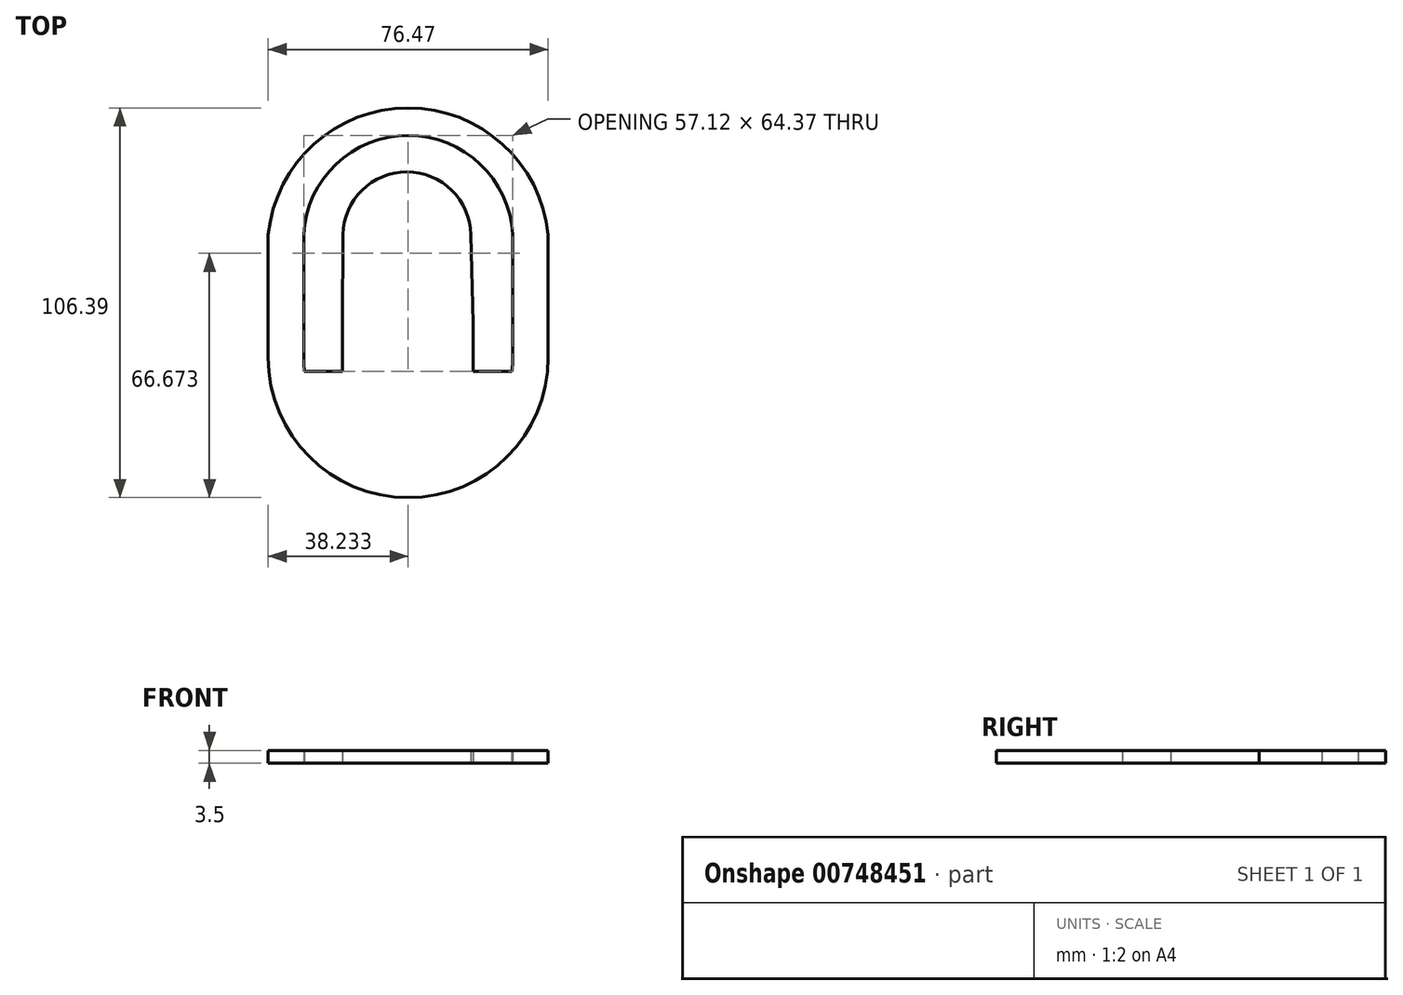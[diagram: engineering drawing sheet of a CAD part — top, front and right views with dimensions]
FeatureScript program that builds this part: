
annotation { "Feature Type Name" : "Feature", "Feature Type Description" : "" }
export const myFeature = defineFeature(function(context is Context, id is Id, definition is map)
    precondition{}
    {
        {
            var Q0;
            Q0=qCreatedBy(makeId("Top.planeOp"),FACE);
            var sketch = newSketch(context, id + "F0", { "sketchPlane" : qUnion([Q0])});
            skArc(sketch, "E0", {"start": v(10.8, 41.88) * mm, "mid": v(-1.53, 54.45) * mm, "end": v(-13.07, 41.16) * mm});
            skLineSegment(sketch, "E1", {"start": v(-13.07, 41.16) * mm, "end": v(-13.07, 17.84) * mm});
            skLineSegment(sketch, "E2", {"start": v(10.8, 41.88) * mm, "end": v(10.22, 17.84) * mm});
            skArc(sketch, "E3", {"start": v(16.28, 41.88) * mm, "mid": v(-1.18, 59.03) * mm, "end": v(-18.64, 41.88) * mm});
            skLineSegment(sketch, "E4", {"start": v(-18.64, 41.88) * mm, "end": v(-18.81, 17.84) * mm});
            skLineSegment(sketch, "E5", {"start": v(16.28, 41.88) * mm, "end": v(16.94, 17.84) * mm});
            skLineSegment(sketch, "E6", {"start": v(-18.81, 17.84) * mm, "end": v(-13.07, 17.84) * mm});
            skLineSegment(sketch, "E7", {"start": v(10.22, 17.84) * mm, "end": v(16.94, 17.84) * mm});
            skArc(sketch, "E8", {"start": v(27.74, 41.88) * mm, "mid": v(-0.82, 68.97) * mm, "end": v(-29.37, 41.88) * mm});
            skLineSegment(sketch, "E9", {"start": v(-29.37, 41.88) * mm, "end": v(-39.05, 41.88) * mm});
            skLineSegment(sketch, "E10", {"start": v(27.74, 41.88) * mm, "end": v(37.42, 41.88) * mm});
            skArc(sketch, "E11", {"start": v(37.42, 41.88) * mm, "mid": v(-0.82, 76.5) * mm, "end": v(-39.05, 41.88) * mm});
            skLineSegment(sketch, "E12", {"start": v(-39.05, 41.88) * mm, "end": v(-39.05, 8.35) * mm});
            skLineSegment(sketch, "E13", {"start": v(37.42, 41.88) * mm, "end": v(37.42, 8.35) * mm});
            skLineSegment(sketch, "E14", {"start": v(27.74, 41.88) * mm, "end": v(27.74, 8.34) * mm});
            skLineSegment(sketch, "E15", {"start": v(27.74, 8.34) * mm, "end": v(37.42, 8.35) * mm});
            skLineSegment(sketch, "E16", {"start": v(-29.37, 41.88) * mm, "end": v(-29.37, 8.35) * mm});
            skLineSegment(sketch, "E17", {"start": v(-29.37, 8.35) * mm, "end": v(-39.05, 8.35) * mm});
            skArc(sketch, "E18", {"start": v(-29.37, 8.35) * mm, "mid": v(-0.82, -20.21) * mm, "end": v(27.74, 8.34) * mm});
            skArc(sketch, "E19", {"start": v(-39.05, 8.35) * mm, "mid": v(-0.82, -29.89) * mm, "end": v(37.42, 8.35) * mm});
            skLineSegment(sketch, "E20", {"start": v(-18.81, 17.84) * mm, "end": v(-18.81, 0) * mm});
            skLineSegment(sketch, "E21", {"start": v(-18.81, 0) * mm, "end": v(-28.13, 0) * mm});
            skLineSegment(sketch, "E22", {"start": v(-13.07, 17.84) * mm, "end": v(-13.07, 0) * mm});
            skLineSegment(sketch, "E23", {"start": v(-13.07, 0) * mm, "end": v(-18.81, 0) * mm});
            skLineSegment(sketch, "E24", {"start": v(-18.81, 4.6) * mm, "end": v(-29.13, 4.6) * mm});
            skLineSegment(sketch, "E25", {"start": v(16.94, 17.84) * mm, "end": v(16.94, 0) * mm});
            skLineSegment(sketch, "E26", {"start": v(10.22, 17.84) * mm, "end": v(10.22, 0) * mm});
            skLineSegment(sketch, "E27", {"start": v(10.22, 0) * mm, "end": v(16.94, 0) * mm});
            skLineSegment(sketch, "E28", {"start": v(-18.81, 4.6) * mm, "end": v(-13.07, 4.6) * mm});
            skPoint(sketch, "E28.endSnap0", {"position": v(-13.07, 8.92) * mm});
            skLineSegment(sketch, "E29", {"start": v(-13.07, 4.6) * mm, "end": v(10.22, 4.6) * mm});
            skLineSegment(sketch, "E30", {"start": v(10.22, 4.6) * mm, "end": v(16.94, 4.6) * mm});
            skLineSegment(sketch, "E31", {"start": v(16.94, 4.6) * mm, "end": v(27.5, 4.6) * mm});
            skLineSegment(sketch, "E32", {"start": v(-13.07, 0) * mm, "end": v(10.22, 0) * mm});
            skLineSegment(sketch, "E33", {"start": v(16.94, 0) * mm, "end": v(26.5, 0) * mm});
            skSolve(sketch);
        }
        {
            var Q0;
            Q0=makeQuery(id+"F0.imprint","IMPRINT",FACE,{"disambiguationData":[TD([[makeQuery(id+"F0.imprint","IMPRINT",EDGE,{"derivedFrom":sQuery(id+"F0.wireOp",EDGE,"E9")}),1.0]])]});
            var Q1;
            Q1=makeQuery(id+"F0.imprint","IMPRINT",FACE,{"disambiguationData":[TD([[makeQuery(id+"F0.imprint","IMPRINT",EDGE,{"derivedFrom":sQuery(id+"F0.wireOp",EDGE,"E8")}),-1.0]])]});
            var Q2;
            Q2=makeQuery(id+"F0.imprint","IMPRINT",FACE,{"disambiguationData":[TD([[makeQuery(id+"F0.imprint","IMPRINT",EDGE,{"derivedFrom":sQuery(id+"F0.wireOp",EDGE,"E10")}),-1.0]])]});
            var Q3;
            {var subQ4=sQuery(id+"F0.wireOp",EDGE,"E15");Q3=makeQuery(id+"F0.imprint","IMPRINT",FACE,{"disambiguationData":[TD([[makeQuery(id+"F0.imprint","IMPRINT",EDGE,{"derivedFrom":subQ4}),-1.0]])]});}
            var Q4;
            {var subQ0=sQuery(id+"F0.wireOp",EDGE,"E31");Q4=makeQuery(id+"F0.imprint","IMPRINT",FACE,{"disambiguationData":[TD([[makeQuery(id+"F0.imprint","IMPRINT",EDGE,{"derivedFrom":subQ0}),-1.0]])]});}
            var Q5;
            {var subQ0=sQuery(id+"F0.wireOp",EDGE,"E27");Q5=makeQuery(id+"F0.imprint","IMPRINT",FACE,{"disambiguationData":[TD([[makeQuery(id+"F0.imprint","IMPRINT",EDGE,{"derivedFrom":subQ0}),1.0]])]});}
            var Q6;
            {var subQ2=sQuery(id+"F0.wireOp",EDGE,"E29");Q6=makeQuery(id+"F0.imprint","IMPRINT",FACE,{"disambiguationData":[TD([[makeQuery(id+"F0.imprint","IMPRINT",EDGE,{"derivedFrom":subQ2}),-1.0]])]});}
            var Q7;
            {var subQ0=sQuery(id+"F0.wireOp",EDGE,"E23");Q7=makeQuery(id+"F0.imprint","IMPRINT",FACE,{"disambiguationData":[TD([[makeQuery(id+"F0.imprint","IMPRINT",EDGE,{"derivedFrom":subQ0}),-1.0]])]});}
            var Q8;
            {var subQ0=sQuery(id+"F0.wireOp",EDGE,"E21");Q8=makeQuery(id+"F0.imprint","IMPRINT",FACE,{"disambiguationData":[TD([[makeQuery(id+"F0.imprint","IMPRINT",EDGE,{"derivedFrom":subQ0}),-1.0]])]});}
            var Q9;
            Q9=makeQuery(id+"F0.imprint","IMPRINT",FACE,{"disambiguationData":[TD([[makeQuery(id+"F0.imprint","IMPRINT",EDGE,{"derivedFrom":sQuery(id+"F0.wireOp",EDGE,"E0")}),-1.0]])]});
            var Q10;
            {var subQ0=sQuery(id+"F0.wireOp",EDGE,"E7");Q10=makeQuery(id+"F0.imprint","IMPRINT",FACE,{"disambiguationData":[TD([[makeQuery(id+"F0.imprint","IMPRINT",EDGE,{"derivedFrom":subQ0}),-1.0]])]});}
            var Q11;
            {var subQ0=sQuery(id+"F0.wireOp",EDGE,"E6");Q11=makeQuery(id+"F0.imprint","IMPRINT",FACE,{"disambiguationData":[TD([[makeQuery(id+"F0.imprint","IMPRINT",EDGE,{"derivedFrom":subQ0}),-1.0]])]});}
            var Q12;
            Q12=makeQuery(id+"F0.imprint","IMPRINT",FACE,{"disambiguationData":[TD([[makeQuery(id+"F0.imprint","IMPRINT",EDGE,{"derivedFrom":sQuery(id+"F0.wireOp",EDGE,"E0")}),1.0]])]});
            var Q13;
            {var subQ0=sQuery(id+"F0.wireOp",EDGE,"E21");Q13=makeQuery(id+"F0.imprint","IMPRINT",FACE,{"disambiguationData":[TD([[makeQuery(id+"F0.imprint","IMPRINT",EDGE,{"derivedFrom":subQ0}),1.0]])]});}
            extrude(context, id + "F1", {"entities" : qUnion([Q0, Q1, Q2, Q3, Q4, Q5, Q6, Q7, Q8, Q9, Q10, Q11, Q12, Q13]), "depth" : 3.5 * mm, "offsetDistance" : 25.4 * mm});
        }
    });
